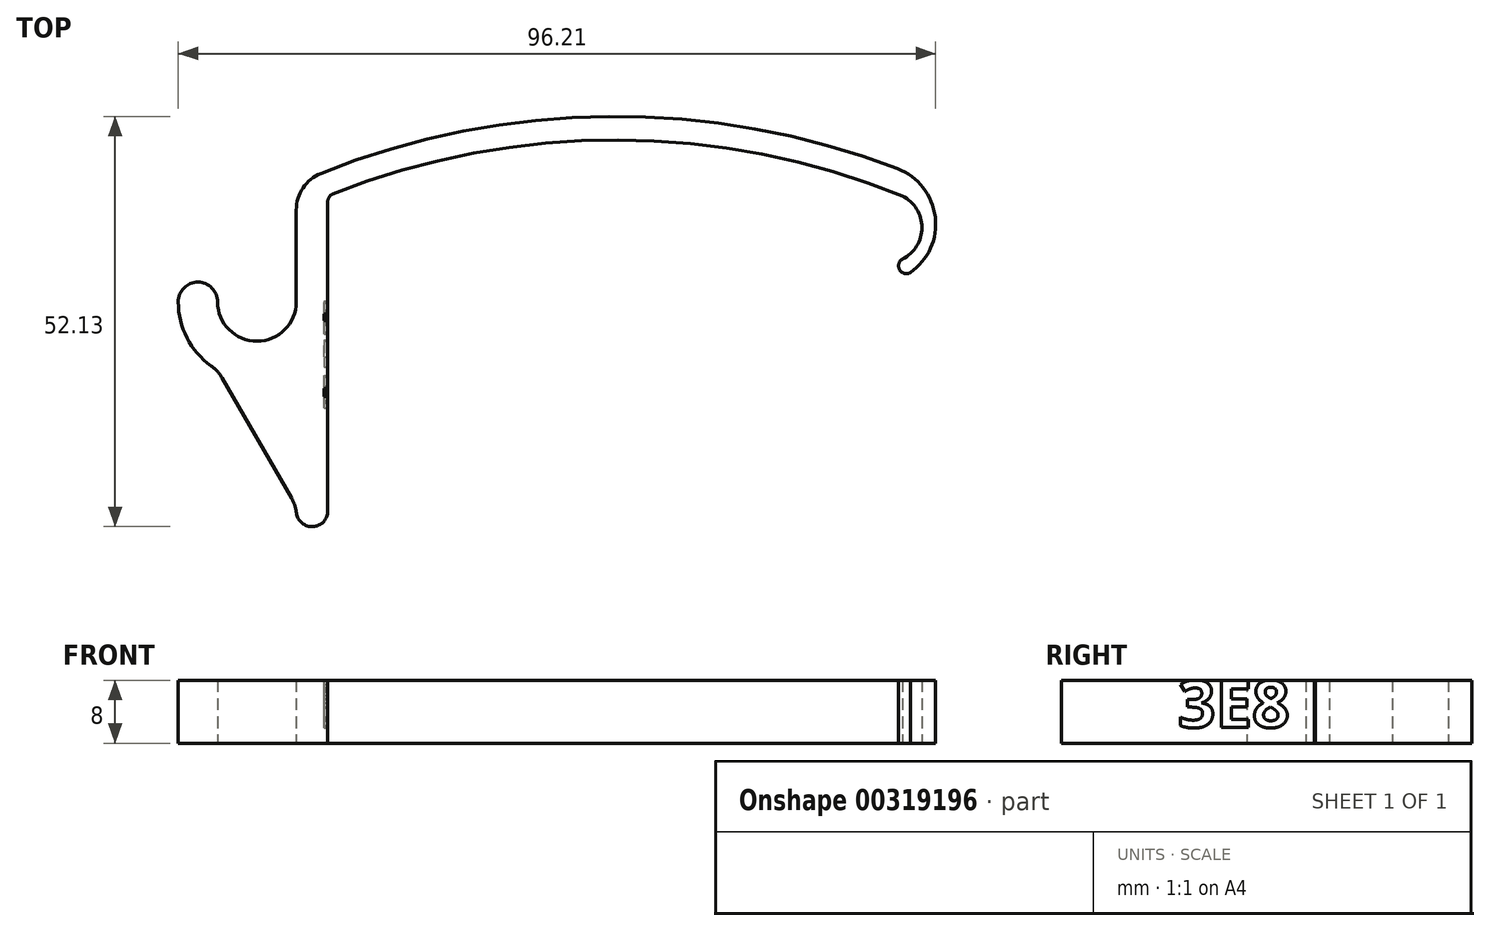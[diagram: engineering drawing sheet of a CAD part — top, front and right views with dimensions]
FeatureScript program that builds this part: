
annotation { "Feature Type Name" : "Feature", "Feature Type Description" : "" }
export const myFeature = defineFeature(function(context is Context, id is Id, definition is map)
    precondition{}
    {
        {
            var Q0;
            Q0=qCreatedBy(makeId("Top.planeOp"),FACE);
            var sketch = newSketch(context, id + "F0", { "sketchPlane" : qUnion([Q0])});
            skLineSegment(sketch, "E0", {"start": v(-36.5, 40) * mm, "end": v(36.5, 40) * mm, "construction": true});
            skLineSegment(sketch, "E1", {"start": v(0, 40) * mm, "end": v(0, 0) * mm, "construction": true});
            skArc(sketch, "E2", {"start": v(36.5, 40) * mm, "mid": v(0, 47.13) * mm, "end": v(-36.5, 40) * mm});
            skArc(sketch, "E3.0", {"start": v(35.89, 43.47) * mm, "mid": v(-2.5, 50.1) * mm, "end": v(-40.5, 41.56) * mm});
            skArc(sketch, "E4", {"start": v(36.5, 32) * mm, "mid": v(38.97, 36) * mm, "end": v(36.5, 40) * mm});
            skArc(sketch, "E5", {"start": v(37.5, 30.27) * mm, "mid": v(40.66, 37.35) * mm, "end": v(35.89, 43.47) * mm});
            skLineSegment(sketch, "E6", {"start": v(-36.5, 40) * mm, "end": v(-36.5, 0) * mm});
            skLineSegment(sketch, "E7", {"start": v(36.5, 40) * mm, "end": v(36.5, 32) * mm, "construction": true});
            skLineSegment(sketch, "E8", {"start": v(36.5, 36) * mm, "end": v(34.5, 36) * mm, "construction": true});
            skLineSegment(sketch, "E9", {"start": v(-40.5, 41.56) * mm, "end": v(-40.5, 26.56) * mm});
            skArc(sketch, "E10", {"start": v(-50.5, 26.56) * mm, "mid": v(-45.5, 21.56) * mm, "end": v(-40.5, 26.56) * mm});
            skArc(sketch, "E11", {"start": v(-50.5, 26.56) * mm, "mid": v(-53, 29.06) * mm, "end": v(-55.5, 26.56) * mm});
            skLineSegment(sketch, "E12", {"start": v(-55.5, 26.56) * mm, "end": v(-50.5, 26.56) * mm, "construction": true});
            skArc(sketch, "E13", {"start": v(-55.5, 26.56) * mm, "mid": v(-50.5, 17.9) * mm, "end": v(-40.5, 17.9) * mm});
            skArc(sketch, "E14", {"start": v(-40.5, 0) * mm, "mid": v(-38.5, -2) * mm, "end": v(-36.5, 0) * mm});
            skLineSegment(sketch, "E15", {"start": v(-40.5, 17.9) * mm, "end": v(-40.5, 0) * mm});
            skArc(sketch, "E16", {"start": v(36.5, 32) * mm, "mid": v(36.13, 30.63) * mm, "end": v(37.5, 30.27) * mm});
            skLineSegment(sketch, "E17", {"start": v(36.5, 32) * mm, "end": v(37.5, 30.27) * mm, "construction": true});
            skSolve(sketch);
        }
        {
            var Q0;
            Q0=qSketchRegion(id+"F0",true);
            extrude(context, id + "F1", {"entities" : qUnion([Q0]), "depth" : 8 * mm});
        }
        {
            var Q0;
            Q0=makeQuery(id+"F1.opExtrude","SWEPT_FACE",FACE,{"disambiguationData":[OSD([sQuery(id+"F0.wireOp",EDGE,"E6")])]});
            var sketch = newSketch(context, id + "F2", { "sketchPlane" : qUnion([Q0])});
            skText(sketch, "E18", { "text": "3E8", "fontName": "OpenSans-Bold.ttf"});
            skLineSegment(sketch, "E19", {"start": v(0, 0) * mm, "end": v(40, 8) * mm, "construction": true});
            skPoint(sketch, "E20", {"position": v(20, 4) * mm});
            const initialGuessF2  = {"E18": [0.01278, 0.002, 1, 0, 0.006]};
            skSetInitialGuess(sketch, initialGuessF2);
            skSolve(sketch);
        }
        {
            var Q0;
            Q0=qSketchRegion(id+"F2",true);
            extrude(context, id + "F3", {"entities" : qUnion([Q0]), "operationType" : NewBodyOperationType.REMOVE, "oppositeDirection" : true, "depth" : .5 * mm});
        }
        {
            var Q0;
            Q0=makeQuery(id+"F1.opExtrude","SWEPT_EDGE",EDGE,{"disambiguationData":[OSD([sQuery(id+"F0.wireOp",EDGE,"E13"),sQuery(id+"F0.wireOp",EDGE,"E15")])]});
            chamfer(context, id + "F4", {"entities" : qUnion([Q0]), "width" : 20 * mm, "tangentPropagation" : true});
        }
        {
            var Q0;
            Q0=makeQuery(id+"F1.opExtrude","SWEPT_EDGE",EDGE,{"disambiguationData":[OSD([sQuery(id+"F0.wireOp",EDGE,"E3.0"),sQuery(id+"F0.wireOp",EDGE,"E9")])]});
            var Q1;
            {var subQ0=sQuery(id+"F0.wireOp",EDGE,"E13");Q1=makeQuery(id+"F4.opChamfer","BLEND_EDGE",EDGE,{"blendedFrom":[makeQuery(id+"F1.opExtrude","SWEPT_EDGE",EDGE,{"disambiguationData":[OSD([subQ0,sQuery(id+"F0.wireOp",EDGE,"E15")])]}),makeQuery(id+"F1.opExtrude","SWEPT_FACE",FACE,{"disambiguationData":[OSD([subQ0])]})],"blendedInto":[makeQuery(id+"F1.opExtrude","SWEPT_FACE",FACE,{"disambiguationData":[OSD([subQ0])]})]});}
            var Q2;
            {var subQ0=sQuery(id+"F0.wireOp",EDGE,"E15");Q2=makeQuery(id+"F4.opChamfer","BLEND_EDGE",EDGE,{"blendedFrom":[makeQuery(id+"F1.opExtrude","SWEPT_EDGE",EDGE,{"disambiguationData":[OSD([sQuery(id+"F0.wireOp",EDGE,"E13"),subQ0])]}),makeQuery(id+"F1.opExtrude","SWEPT_FACE",FACE,{"disambiguationData":[OSD([subQ0])]})],"blendedInto":[makeQuery(id+"F1.opExtrude","SWEPT_FACE",FACE,{"disambiguationData":[OSD([subQ0])]})]});}
            fillet(context, id + "F5", {"entities" : qUnion([Q0, Q1, Q2]), "radius" : 5 * mm, "tangentPropagation" : true, "allowEdgeOverflow" : false});
        }
        {
            var Q0;
            Q0=makeQuery(id+"F1.opExtrude","SWEPT_EDGE",EDGE,{"disambiguationData":[OSD([sQuery(id+"F0.wireOp",EDGE,"E2"),sQuery(id+"F0.wireOp",EDGE,"E6")])]});
            fillet(context, id + "F6", {"entities" : qUnion([Q0]), "radius" : 1 * mm, "tangentPropagation" : true, "allowEdgeOverflow" : false});
        }
    });
